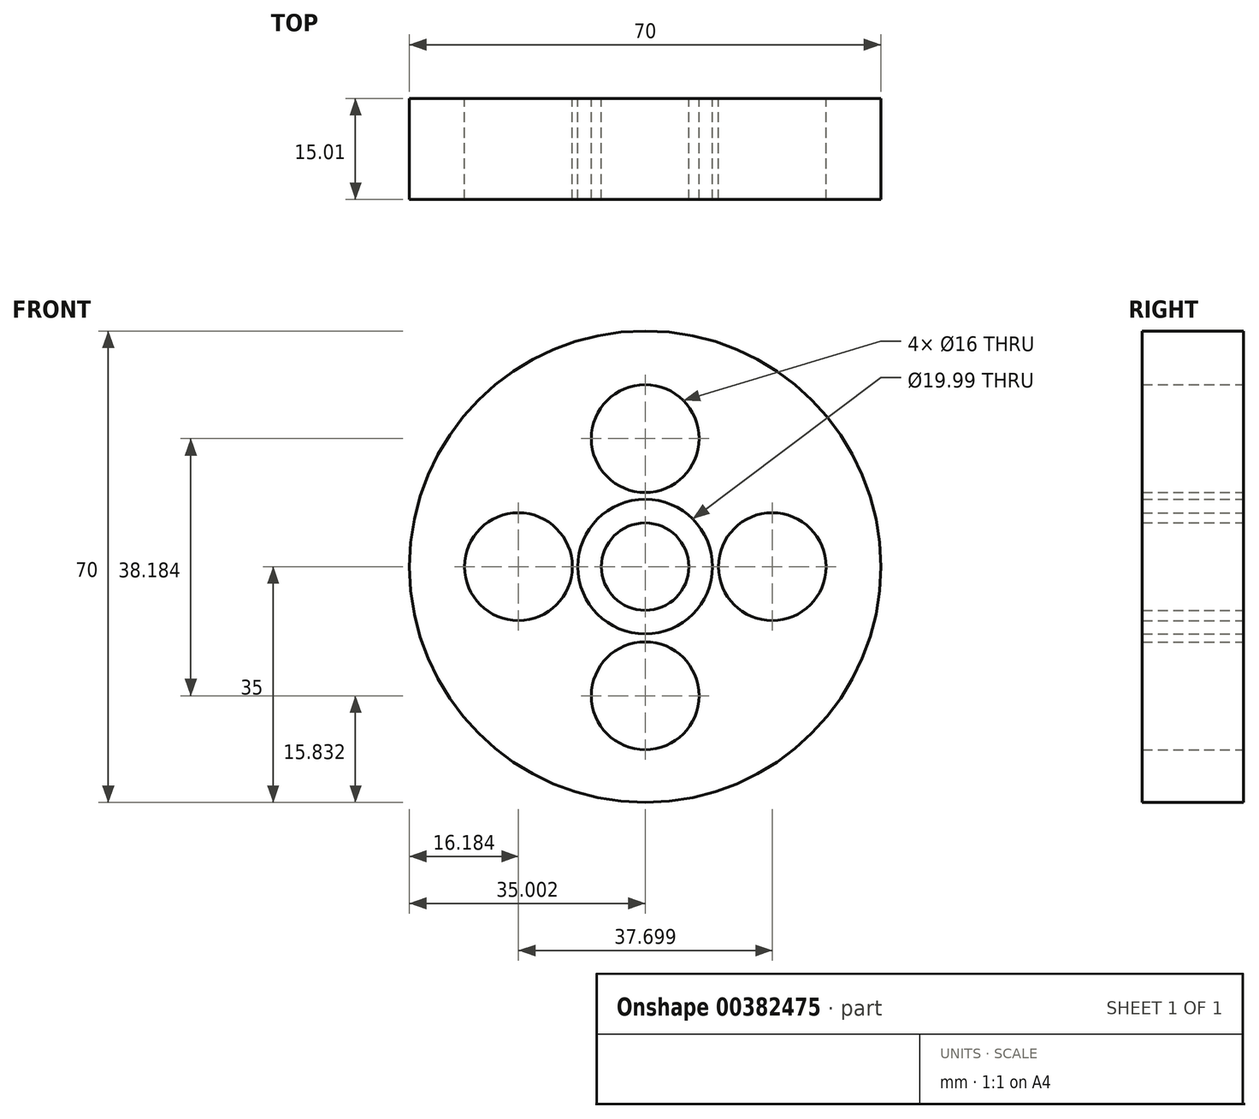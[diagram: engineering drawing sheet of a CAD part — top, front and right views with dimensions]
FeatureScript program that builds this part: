
annotation { "Feature Type Name" : "Feature", "Feature Type Description" : "" }
export const myFeature = defineFeature(function(context is Context, id is Id, definition is map)
    precondition{}
    {
        {
            var Q0;
            Q0=qCreatedBy(makeId("Front.planeOp"),FACE);
            var sketch = newSketch(context, id + "F0", { "sketchPlane" : qUnion([Q0])});
            skCircle(sketch, "E0", {"center": v(34.26, 0) * mm, "radius": 35 * mm});
            skCircle(sketch, "E1", {"center": v(34.26, 0) * mm, "radius": 30 * mm});
            skCircle(sketch, "E2", {"center": v(34.26, 0) * mm, "radius": 10 * mm});
            skCircle(sketch, "E3", {"center": v(34.26, 0) * mm, "radius": 6.5 * mm});
            skCircle(sketch, "E4", {"center": v(34.26, -19.17) * mm, "radius": 8 * mm});
            skCircle(sketch, "E5", {"center": v(15.44, 0) * mm, "radius": 8 * mm});
            skCircle(sketch, "E6", {"center": v(34.26, 19.02) * mm, "radius": 8 * mm});
            skCircle(sketch, "E7", {"center": v(53.14, 0) * mm, "radius": 8 * mm});
            skSolve(sketch);
        }
        {
            var Q0;
            Q0=makeQuery(id+"F0.imprint","IMPRINT",FACE,{"disambiguationData":[TD([[makeQuery(id+"F0.imprint","IMPRINT",EDGE,{"derivedFrom":sQuery(id+"F0.wireOp",EDGE,"E1")}),1.0]])]});
            var Q1;
            Q1=makeQuery(id+"F0.imprint","IMPRINT",FACE,{"disambiguationData":[TD([[makeQuery(id+"F0.imprint","IMPRINT",EDGE,{"derivedFrom":sQuery(id+"F0.wireOp",EDGE,"E0")}),1.0]])]});
            var Q2;
            Q2=makeQuery(id+"F0.imprint","IMPRINT",FACE,{"disambiguationData":[TD([[makeQuery(id+"F0.imprint","IMPRINT",EDGE,{"derivedFrom":sQuery(id+"F0.wireOp",EDGE,"E3")}),1.0]])]});
            extrude(context, id + "F1", {"entities" : qUnion([Q0, Q1, Q2]), "depth" : 15 * mm});
        }
    });
